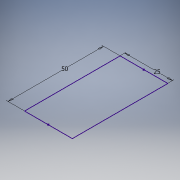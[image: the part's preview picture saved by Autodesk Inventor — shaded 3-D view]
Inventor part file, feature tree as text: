
AUTODESK INVENTOR PART (.ipt)
format: ipt  version: 2018 (Build 220112000, 112)  size: 87,552 bytes
history: native  units: mm
features: sketch x1
ambient origin geometry x8: Origin, YZ Plane, XZ Plane, XY Plane, X Axis, Y Axis, Z Axis, Center Point
feature tree (1):
  sketch  "Sketch1"  dims[d0=25.0mm d1=50.0mm]
